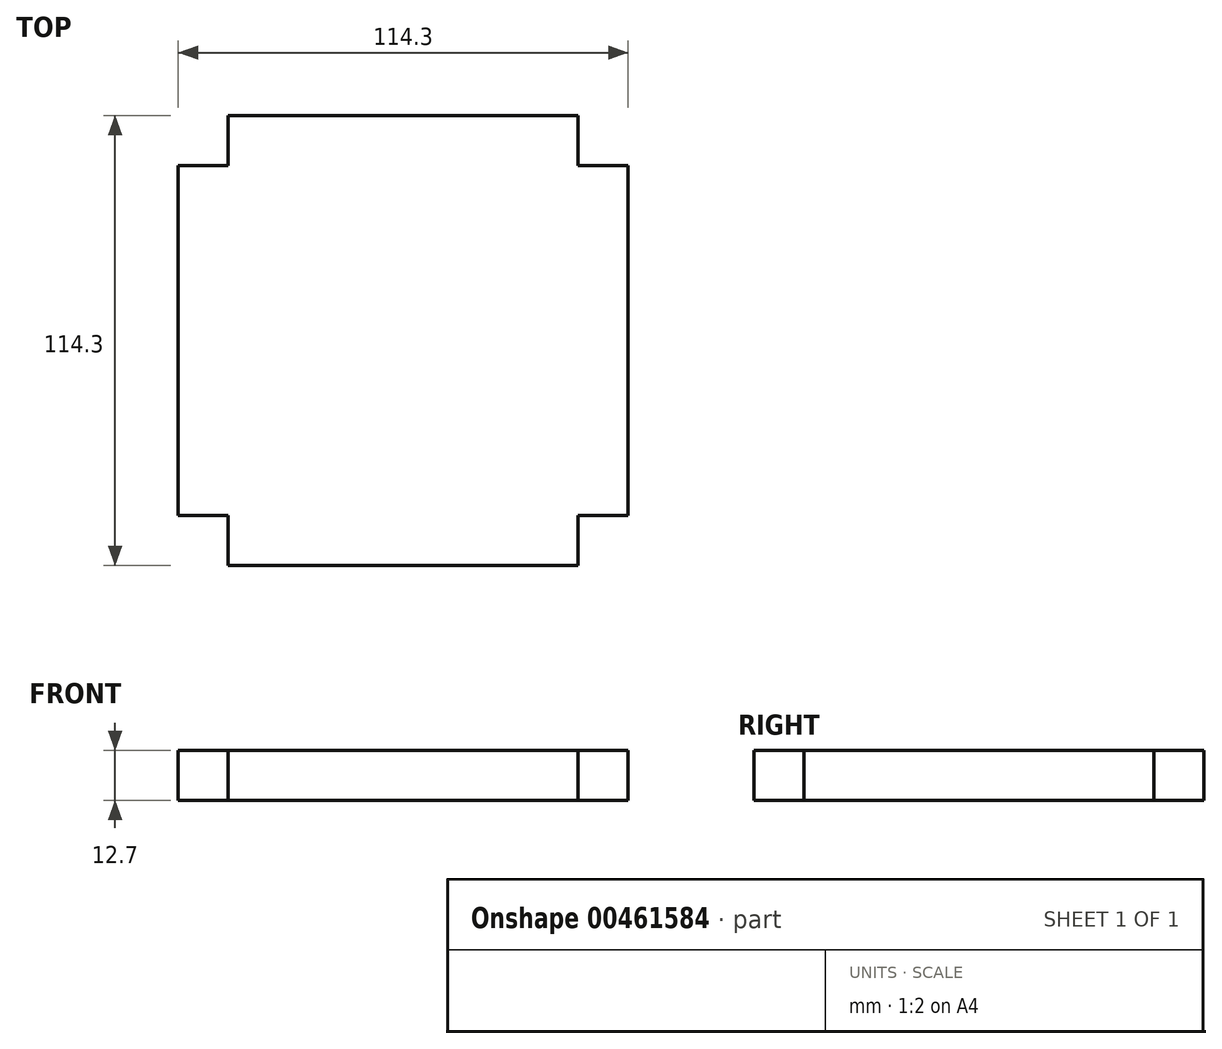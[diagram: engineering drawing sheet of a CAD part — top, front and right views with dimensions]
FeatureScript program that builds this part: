
annotation { "Feature Type Name" : "Feature", "Feature Type Description" : "" }
export const myFeature = defineFeature(function(context is Context, id is Id, definition is map)
    precondition{}
    {
        {
            var Q0;
            Q0=qCreatedBy(makeId("Top.planeOp"),FACE);
            var sketch = newSketch(context, id + "F0", { "sketchPlane" : qUnion([Q0])});
            skLineSegment(sketch, "E0.bottom", {"start": v(-44.45, 57.15) * mm, "end": v(44.45, 57.15) * mm});
            skLineSegment(sketch, "E0.top", {"start": v(-44.45, -57.15) * mm, "end": v(44.45, -57.15) * mm});
            skLineSegment(sketch, "E0.left", {"start": v(-44.45, 57.15) * mm, "end": v(-44.45, -57.15) * mm});
            skLineSegment(sketch, "E0.right", {"start": v(44.45, 57.15) * mm, "end": v(44.45, -57.15) * mm});
            skPoint(sketch, "E0.middle", {"position": v(0, 0) * mm});
            skLineSegment(sketch, "E1", {"start": v(-44.45, -44.45) * mm, "end": v(-57.15, -44.45) * mm});
            skLineSegment(sketch, "E2", {"start": v(-57.15, -44.45) * mm, "end": v(-57.15, 44.45) * mm});
            skLineSegment(sketch, "E3", {"start": v(-57.15, 44.45) * mm, "end": v(-44.45, 44.45) * mm});
            skLineSegment(sketch, "E4", {"start": v(-44.45, 44.45) * mm, "end": v(57.15, 44.45) * mm});
            skLineSegment(sketch, "E5", {"start": v(57.15, 44.45) * mm, "end": v(57.15, -44.45) * mm});
            skLineSegment(sketch, "E6", {"start": v(57.15, -44.45) * mm, "end": v(44.45, -44.45) * mm});
            skSolve(sketch);
        }
        {
            var Q0;
            Q0 = qSketchRegion(id + "F0", true);
            extrude(context, id + "F1", {"entities" : qUnion([Q0]), "depth" : 12.7 * mm});
        }
    });
